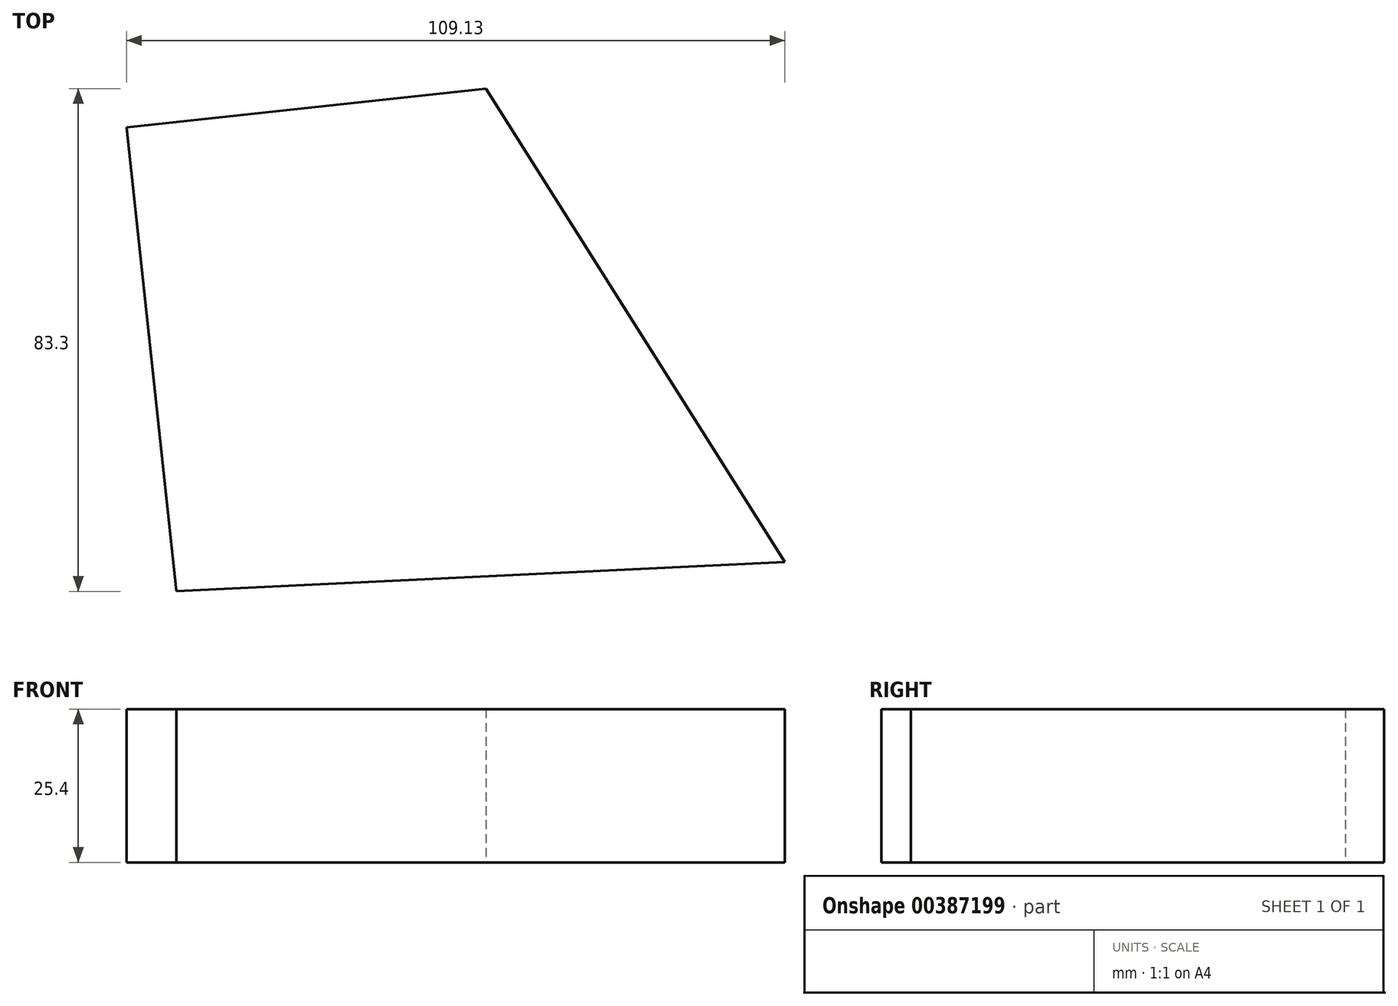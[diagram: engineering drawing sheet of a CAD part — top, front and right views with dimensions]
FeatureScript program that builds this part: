
annotation { "Feature Type Name" : "Feature", "Feature Type Description" : "" }
export const myFeature = defineFeature(function(context is Context, id is Id, definition is map)
    precondition{}
    {
        {
            var Q0;
            Q0=qCreatedBy(makeId("Top.planeOp"),FACE);
            var sketch = newSketch(context, id + "F0", { "sketchPlane" : qUnion([Q0])});
            skLineSegment(sketch, "E0", {"start": v(-123.13, -42.43) * mm, "end": v(-131.4, 34.46) * mm});
            skLineSegment(sketch, "E1", {"start": v(-131.4, 34.46) * mm, "end": v(-71.81, 40.87) * mm});
            skLineSegment(sketch, "E2", {"start": v(-71.81, 40.87) * mm, "end": v(-22.27, -37.6) * mm});
            skLineSegment(sketch, "E3", {"start": v(-22.27, -37.6) * mm, "end": v(-123.13, -42.43) * mm});
            skSolve(sketch);
        }
        {
            var Q0;
            Q0=makeQuery(id+"F0.imprint","IMPRINT",FACE,{"disambiguationData":[TD([[makeQuery(id+"F0.imprint","IMPRINT",EDGE,{"derivedFrom":sQuery(id+"F0.wireOp",EDGE,"E0")}),-1.0]])]});
            extrude(context, id + "F1", {"entities" : qUnion([Q0]), "depth" : 25.4 * mm});
        }
    });
